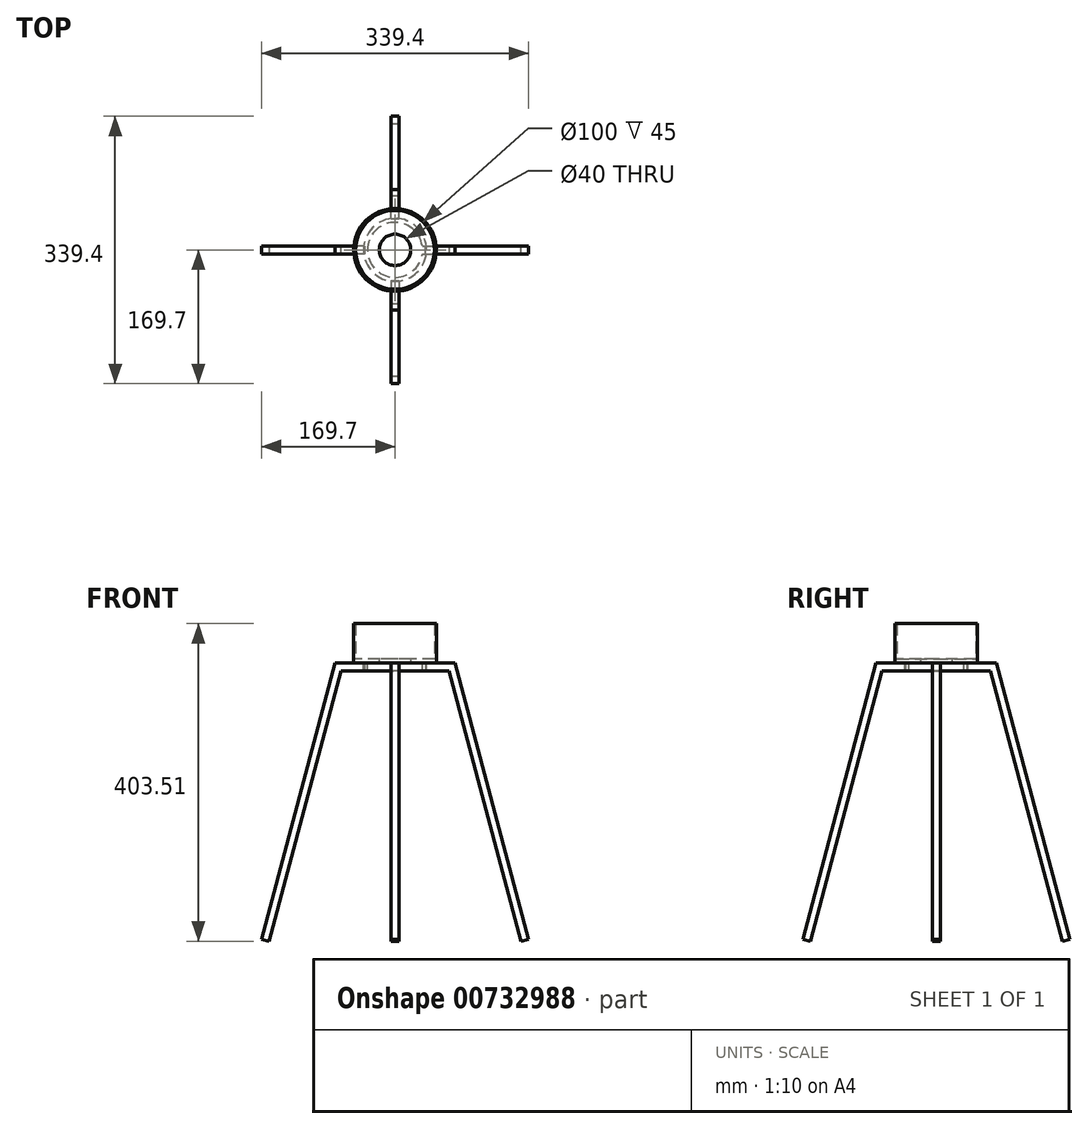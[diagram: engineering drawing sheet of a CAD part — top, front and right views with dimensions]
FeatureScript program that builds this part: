
annotation { "Feature Type Name" : "Feature", "Feature Type Description" : "" }
export const myFeature = defineFeature(function(context is Context, id is Id, definition is map)
    precondition{}
    {
        {
            var Q0;
            Q0=qCreatedBy(makeId("Top.planeOp"),FACE);
            var sketch = newSketch(context, id + "F0", { "sketchPlane" : qUnion([Q0])});
            skCircle(sketch, "E0", {"center": v(0, 0) * mm, "radius": 50 * mm});
            skCircle(sketch, "E1", {"center": v(0, 0) * mm, "radius": 52.5 * mm});
            skSolve(sketch);
        }
        {
            var Q0;
            Q0=makeQuery(id+"F0.imprint","IMPRINT",FACE,{"disambiguationData":[TD([[makeQuery(id+"F0.imprint","IMPRINT",EDGE,{"derivedFrom":sQuery(id+"F0.wireOp",EDGE,"E0")}),1.0]])]});
            extrude(context, id + "F1", {"entities" : qUnion([Q0]), "depth" : 5 * mm, "offsetDistance" : 25 * mm});
        }
        {
            var Q0;
            Q0 = qSketchRegion(id + "F0", true);
            extrude(context, id + "F2", {"entities" : qUnion([Q0]), "operationType" : NewBodyOperationType.ADD, "depth" : 50 * mm, "offsetDistance" : 25 * mm});
        }
        {
            var Q0;
            {var subQ0=sQuery(id+"F0.wireOp",EDGE,"E0");Q0=makeQuery(id+"F2.boolean.opBoolean","MERGE",FACE,{"derivedFrom":[makeQuery(id+"F1.opExtrude","CAP_FACE",FACE,{"disambiguationData":[OSD([subQ0])],"isStart":true}),makeQuery(id+"F2.opExtrude","CAP_FACE",FACE,{"disambiguationData":[OSD([subQ0,sQuery(id+"F0.wireOp",EDGE,"E1")])],"isStart":true})]});}
            var sketch = newSketch(context, id + "F3", { "sketchPlane" : qUnion([Q0])});
            skCircle(sketch, "E2", {"center": v(0, 0) * mm, "radius": 20 * mm});
            skSolve(sketch);
        }
        {
            var Q0;
            Q0 = qSketchRegion(id + "F3", true);
            extrude(context, id + "F4", {"entities" : qUnion([Q0]), "operationType" : NewBodyOperationType.REMOVE, "endBound" : BoundingType.UP_TO_NEXT, "oppositeDirection" : true, "depth" : 25 * mm, "offsetDistance" : 25 * mm});
        }
        {
            var Q0;
            {var subQ0=sQuery(id+"F0.wireOp",EDGE,"E0");Q0=makeQuery(id+"F2.boolean.opBoolean","MERGE",FACE,{"derivedFrom":[makeQuery(id+"F1.opExtrude","CAP_FACE",FACE,{"disambiguationData":[OSD([subQ0])],"isStart":true}),makeQuery(id+"F2.opExtrude","CAP_FACE",FACE,{"disambiguationData":[OSD([subQ0,sQuery(id+"F0.wireOp",EDGE,"E1")])],"isStart":true})]});}
            var sketch = newSketch(context, id + "F5", { "sketchPlane" : qUnion([Q0])});
            skCircle(sketch, "E3", {"center": v(0, 0) * mm, "radius": 35 * mm});
            skCircle(sketch, "E4", {"center": v(0, 0) * mm, "radius": 40 * mm});
            skSolve(sketch);
        }
        {
            var Q0;
            Q0 = qSketchRegion(id + "F5", true);
            extrude(context, id + "F6", {"entities" : qUnion([Q0]), "operationType" : NewBodyOperationType.ADD, "depth" : 10 * mm, "offsetDistance" : 25 * mm});
        }
        {
            var Q0;
            Q0=qCreatedBy(makeId("Right.planeOp"),FACE);
            var sketch = newSketch(context, id + "F7", { "sketchPlane" : qUnion([Q0])});
            skLineSegment(sketch, "E5.bottom", {"start": v(-5, 0) * mm, "end": v(5, 0) * mm});
            skLineSegment(sketch, "E5.top", {"start": v(-5, -10) * mm, "end": v(5, -10) * mm});
            skLineSegment(sketch, "E5.left", {"start": v(-5, 0) * mm, "end": v(-5, -10) * mm});
            skLineSegment(sketch, "E5.right", {"start": v(5, 0) * mm, "end": v(5, -10) * mm});
            skSolve(sketch);
        }
        {
            var Q0;
            Q0=qCreatedBy(makeId("Front.planeOp"),FACE);
            var sketch = newSketch(context, id + "F8", { "sketchPlane" : qUnion([Q0])});
            skLineSegment(sketch, "E6", {"start": v(38.95, -3.92) * mm, "end": v(73.44, -3.92) * mm});
            skLineSegment(sketch, "E7", {"start": v(73.44, -3.92) * mm, "end": v(175.92, -389.59) * mm});
            skSolve(sketch);
        }
        {
            var Q0;
            Q0=makeQuery(id+"F7.imprint","IMPRINT",FACE,{"disambiguationData":[TD([[makeQuery(id+"F7.imprint","IMPRINT",EDGE,{"derivedFrom":sQuery(id+"F7.wireOp",EDGE,"E5.bottom")}),-1.0]])]});
            var Q1;
            Q1=sQuery(id+"F8.wireOp",EDGE,"E6");
            var Q2;
            Q2=sQuery(id+"F8.wireOp",EDGE,"E7");
            sweep(context, id + "F9", {"profiles" : qUnion([Q0]), "path" : qUnion([Q1, Q2])});
        }
        {
            var Q0;
            Q0=makeQuery(id+"F9.opSweep","SWEPT_FACE",FACE,{"disambiguationData":[OSD([sQuery(id+"F7.wireOp",EDGE,"E5.top"),sQuery(id+"F8.wireOp",EDGE,"E6")])]});
            var sketch = newSketch(context, id + "F10", { "sketchPlane" : qUnion([Q0])});
            skLineSegment(sketch, "E8.bottom", {"start": v(0, 5) * mm, "end": v(39, 5) * mm});
            skLineSegment(sketch, "E8.top", {"start": v(0, -5) * mm, "end": v(39, -5) * mm});
            skLineSegment(sketch, "E8.left", {"start": v(0, 5) * mm, "end": v(0, -5) * mm});
            skLineSegment(sketch, "E8.right", {"start": v(39, 5) * mm, "end": v(39, -5) * mm});
            skSolve(sketch);
        }
        {
            var Q0;
            Q0 = qSketchRegion(id + "F10", true);
            extrude(context, id + "F11", {"entities" : qUnion([Q0]), "operationType" : NewBodyOperationType.REMOVE, "endBound" : BoundingType.UP_TO_NEXT, "oppositeDirection" : true, "depth" : 25 * mm, "offsetDistance" : 25 * mm});
        }
        {
            var Q0;
            Q0=makeQuery(id+"F9.opSweep","SWEPT_BODY",BODY,{"disambiguationData":[OSD([sQuery(id+"F7.wireOp",EDGE,"E5.bottom"),sQuery(id+"F7.wireOp",EDGE,"E5.top"),sQuery(id+"F7.wireOp",EDGE,"E5.left"),sQuery(id+"F7.wireOp",EDGE,"E5.right"),sQuery(id+"F8.wireOp",EDGE,"E7")])]});
            var Q1;
            Q1=makeQuery(id+"F6.opExtrude","CAP_EDGE",EDGE,{"disambiguationData":[OSD([sQuery(id+"F5.wireOp",EDGE,"E4")])],"isStart":false});
            circularPattern(context, id + "F12", {"entities" : qUnion([Q0]), "axis" : qUnion([Q1]), "angle" : 360 * degree, "instanceCount" : 4, "equalSpace" : true});
        }
    });
